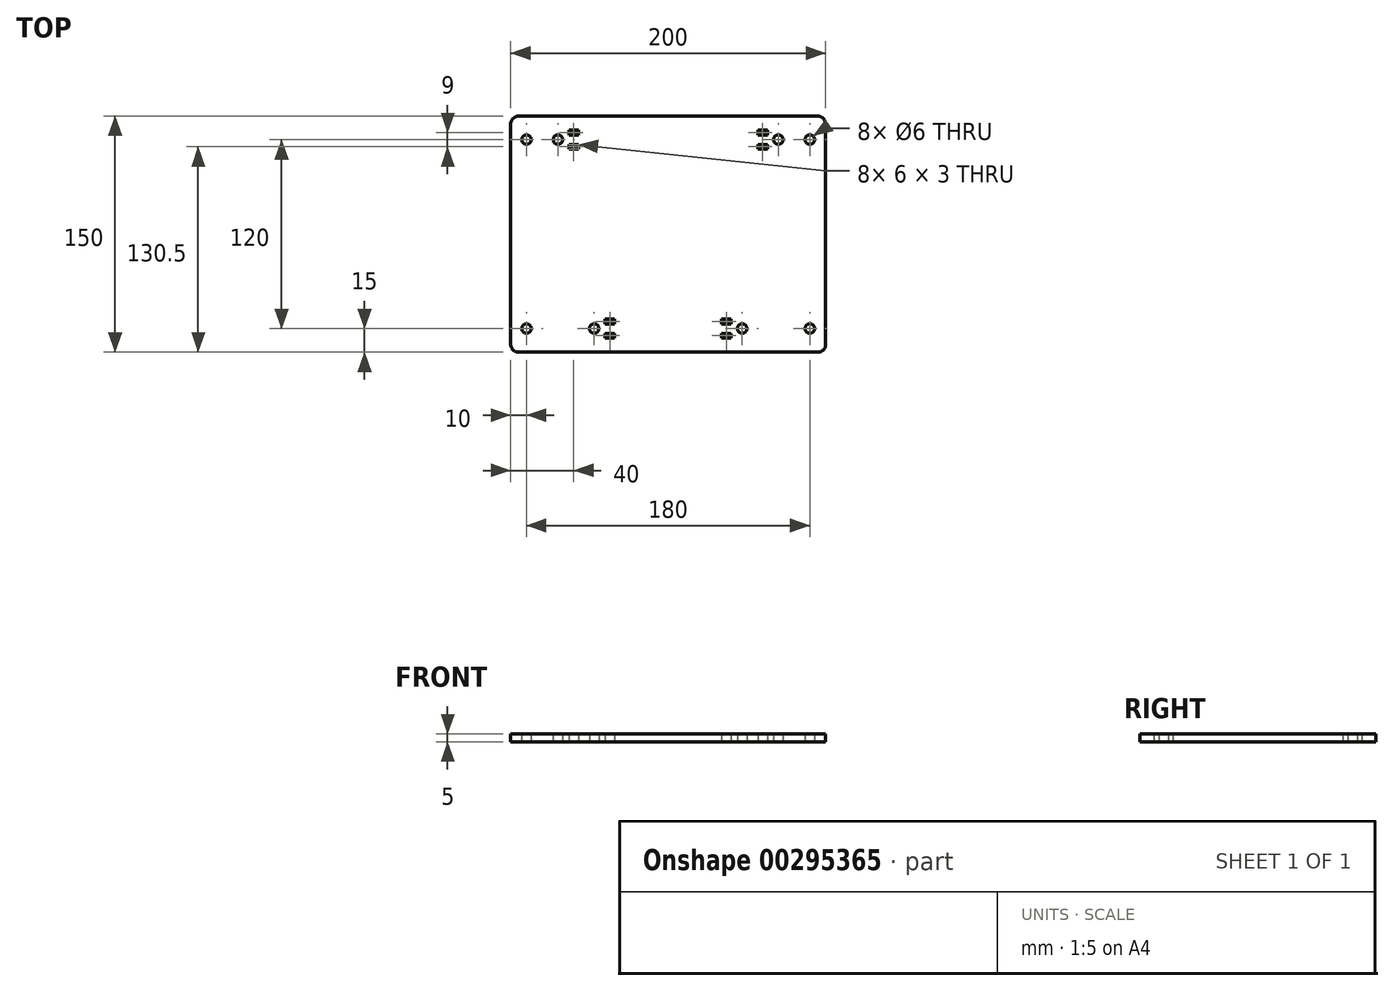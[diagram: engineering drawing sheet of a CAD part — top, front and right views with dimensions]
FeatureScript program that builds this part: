
annotation { "Feature Type Name" : "Feature", "Feature Type Description" : "" }
export const myFeature = defineFeature(function(context is Context, id is Id, definition is map)
    precondition{}
    {
        {
            var Q0;
            Q0=qCreatedBy(makeId("Top.planeOp"),FACE);
            var sketch = newSketch(context, id + "F0", { "sketchPlane" : qUnion([Q0])});
            skCircle(sketch, "E0", {"center": v(-70, 60) * mm, "radius": 3 * mm});
            skCircle(sketch, "E1.MirrorC", {"center": v(70, 60) * mm, "radius": 3 * mm});
            skCircle(sketch, "E2", {"center": v(-47, -60) * mm, "radius": 3 * mm});
            skCircle(sketch, "E3.MirrorC", {"center": v(47, -60) * mm, "radius": 3 * mm});
            skLineSegment(sketch, "E4.top", {"start": v(95, 75) * mm, "end": v(-95, 75) * mm});
            skLineSegment(sketch, "E4.left", {"start": v(100, -70) * mm, "end": v(100, 70) * mm});
            skLineSegment(sketch, "E4.right", {"start": v(-100, -70) * mm, "end": v(-100, 70) * mm});
            skLineSegment(sketch, "E5", {"start": v(-95, -75) * mm, "end": v(95, -75) * mm});
            skPoint(sketch, "E6.positionSnap0", {"position": v(100, 0) * mm});
            skPoint(sketch, "E6.positionSnap1", {"position": v(0, 75) * mm});
            skLineSegment(sketch, "E7.bottom", {"start": v(-63, 66) * mm, "end": v(-57, 66) * mm});
            skLineSegment(sketch, "E7.top", {"start": v(-63, 63) * mm, "end": v(-57, 63) * mm});
            skLineSegment(sketch, "E7.left", {"start": v(-63, 66) * mm, "end": v(-63, 63) * mm});
            skLineSegment(sketch, "E7.right", {"start": v(-57, 66) * mm, "end": v(-57, 63) * mm});
            skLineSegment(sketch, "E8.bottom", {"start": v(-63, 57) * mm, "end": v(-57, 57) * mm});
            skLineSegment(sketch, "E8.top", {"start": v(-63, 54) * mm, "end": v(-57, 54) * mm});
            skLineSegment(sketch, "E8.left", {"start": v(-63, 57) * mm, "end": v(-63, 54) * mm});
            skLineSegment(sketch, "E8.right", {"start": v(-57, 57) * mm, "end": v(-57, 54) * mm});
            skLineSegment(sketch, "E9.bottom", {"start": v(-40, -54) * mm, "end": v(-34, -54) * mm});
            skLineSegment(sketch, "E9.top", {"start": v(-40, -57) * mm, "end": v(-34, -57) * mm});
            skLineSegment(sketch, "E9.left", {"start": v(-40, -54) * mm, "end": v(-40, -57) * mm});
            skLineSegment(sketch, "E9.right", {"start": v(-34, -54) * mm, "end": v(-34, -57) * mm});
            skLineSegment(sketch, "E10.bottom", {"start": v(-40, -63) * mm, "end": v(-34, -63) * mm});
            skLineSegment(sketch, "E10.top", {"start": v(-40, -66) * mm, "end": v(-34, -66) * mm});
            skLineSegment(sketch, "E10.left", {"start": v(-40, -63) * mm, "end": v(-40, -66) * mm});
            skLineSegment(sketch, "E10.right", {"start": v(-34, -63) * mm, "end": v(-34, -66) * mm});
            skLineSegment(sketch, "E11.bottom", {"start": v(57, 66) * mm, "end": v(63, 66) * mm});
            skLineSegment(sketch, "E11.top", {"start": v(57, 63) * mm, "end": v(63, 63) * mm});
            skLineSegment(sketch, "E11.left", {"start": v(57, 66) * mm, "end": v(57, 63) * mm});
            skLineSegment(sketch, "E11.right", {"start": v(63, 66) * mm, "end": v(63, 63) * mm});
            skLineSegment(sketch, "E12.bottom", {"start": v(57, 57) * mm, "end": v(63, 57) * mm});
            skLineSegment(sketch, "E12.top", {"start": v(57, 54) * mm, "end": v(63, 54) * mm});
            skLineSegment(sketch, "E12.left", {"start": v(57, 57) * mm, "end": v(57, 54) * mm});
            skLineSegment(sketch, "E12.right", {"start": v(63, 57) * mm, "end": v(63, 54) * mm});
            skLineSegment(sketch, "E13.bottom", {"start": v(34, -54) * mm, "end": v(40, -54) * mm});
            skLineSegment(sketch, "E13.top", {"start": v(34, -57) * mm, "end": v(40, -57) * mm});
            skLineSegment(sketch, "E13.left", {"start": v(34, -54) * mm, "end": v(34, -57) * mm});
            skLineSegment(sketch, "E13.right", {"start": v(40, -54) * mm, "end": v(40, -57) * mm});
            skLineSegment(sketch, "E14.bottom", {"start": v(34, -63) * mm, "end": v(40, -63) * mm});
            skLineSegment(sketch, "E14.top", {"start": v(34, -66) * mm, "end": v(40, -66) * mm});
            skLineSegment(sketch, "E14.left", {"start": v(34, -63) * mm, "end": v(34, -66) * mm});
            skLineSegment(sketch, "E14.right", {"start": v(40, -63) * mm, "end": v(40, -66) * mm});
            skPoint(sketch, "E15.visualSharp", {"position": v(-100, 75) * mm});
            skArc(sketch, "E15.filletArc", {"start": v(-95, 75) * mm, "mid": v(-98.54, 73.54) * mm, "end": v(-100, 70) * mm});
            skPoint(sketch, "E16.visualSharp", {"position": v(100, 75) * mm});
            skArc(sketch, "E16.filletArc", {"start": v(100, 70) * mm, "mid": v(98.54, 73.54) * mm, "end": v(95, 75) * mm});
            skPoint(sketch, "E17.visualSharp", {"position": v(100, -75) * mm});
            skArc(sketch, "E17.filletArc", {"start": v(95, -75) * mm, "mid": v(98.54, -73.54) * mm, "end": v(100, -70) * mm});
            skPoint(sketch, "E18.visualSharp", {"position": v(-100, -75) * mm});
            skArc(sketch, "E18.filletArc", {"start": v(-100, -70) * mm, "mid": v(-98.54, -73.54) * mm, "end": v(-95, -75) * mm});
            skCircle(sketch, "E19", {"center": v(-90, 60) * mm, "radius": 3 * mm});
            skCircle(sketch, "E20", {"center": v(90, 60) * mm, "radius": 3 * mm});
            skCircle(sketch, "E21", {"center": v(-90, -60) * mm, "radius": 3 * mm});
            skCircle(sketch, "E22", {"center": v(90, -60) * mm, "radius": 3 * mm});
            skSolve(sketch);
        }
        {
            var Q0;
            Q0=makeQuery(id+"F0.imprint","IMPRINT",FACE,{"disambiguationData":[TD([[makeQuery(id+"F0.imprint","IMPRINT",EDGE,{"derivedFrom":sQuery(id+"F0.wireOp",EDGE,"E0")}),-1.0]])]});
            extrude(context, id + "F1", {"entities" : qUnion([Q0]), "depth" : 5 * mm});
        }
    });
